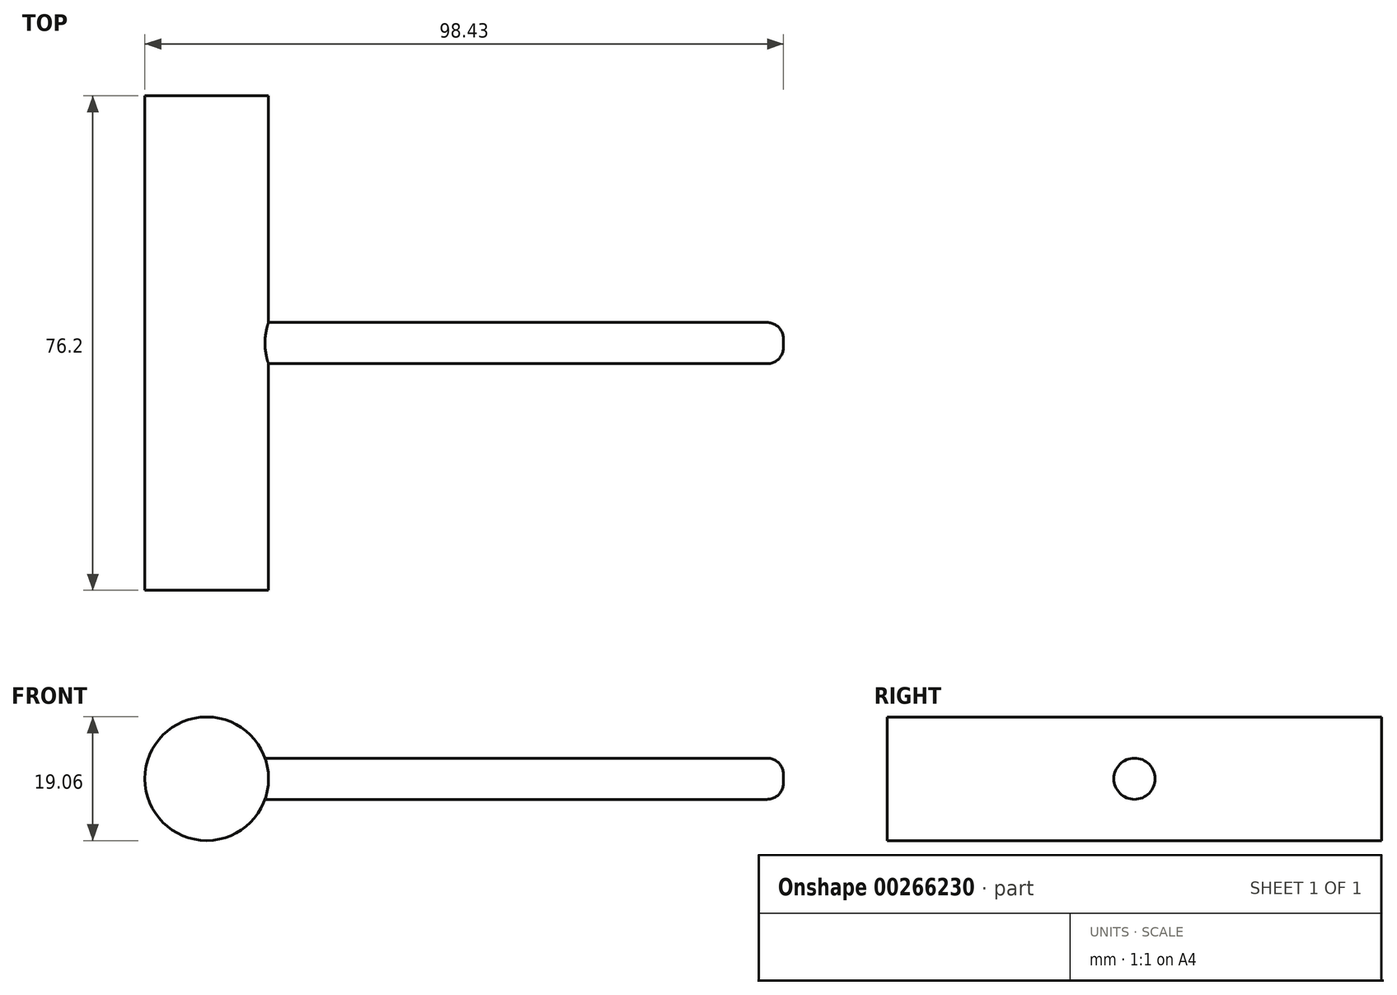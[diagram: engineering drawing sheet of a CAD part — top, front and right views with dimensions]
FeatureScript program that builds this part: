
annotation { "Feature Type Name" : "Feature", "Feature Type Description" : "" }
export const myFeature = defineFeature(function(context is Context, id is Id, definition is map)
    precondition{}
    {
        {
            var Q0;
            Q0=qCreatedBy(makeId("Front.planeOp"),FACE);
            var sketch = newSketch(context, id + "F0", { "sketchPlane" : qUnion([Q0])});
            skCircle(sketch, "E0", {"center": v(0, 0) * mm, "radius": 9.53 * mm});
            skSolve(sketch);
        }
        {
            var Q0;
            Q0=makeQuery(id+"F0.imprint","IMPRINT",FACE,{"disambiguationData":[TD([[makeQuery(id+"F0.imprint","IMPRINT",EDGE,{"derivedFrom":sQuery(id+"F0.wireOp",EDGE,"E0")}),1.0]])]});
            extrude(context, id + "F1", {"entities" : qUnion([Q0]), "oppositeDirection" : true, "depth" : 76.2 * mm});
        }
        {
            var Q0;
            Q0=qCreatedBy(makeId("Right.planeOp"),FACE);
            var sketch = newSketch(context, id + "F2", { "sketchPlane" : qUnion([Q0])});
            skCircle(sketch, "E1", {"center": v(38.1, 0) * mm, "radius": 3.18 * mm});
            skSolve(sketch);
        }
        {
            var Q0;
            Q0 = qSketchRegion(id + "F2", true);
            extrude(context, id + "F3", {"entities" : qUnion([Q0]), "operationType" : NewBodyOperationType.ADD, "depth" : 88.9 * mm});
        }
        {
            var Q0;
            Q0=makeQuery(id+"F3.opExtrude","CAP_EDGE",EDGE,{"disambiguationData":[OSD([sQuery(id+"F2.wireOp",EDGE,"E1")])],"isStart":false});
            fillet(context, id + "F4", {"entities" : qUnion([Q0]), "radius" : 2.54 * mm, "tangentPropagation" : true, "allowEdgeOverflow" : false});
        }
    });
